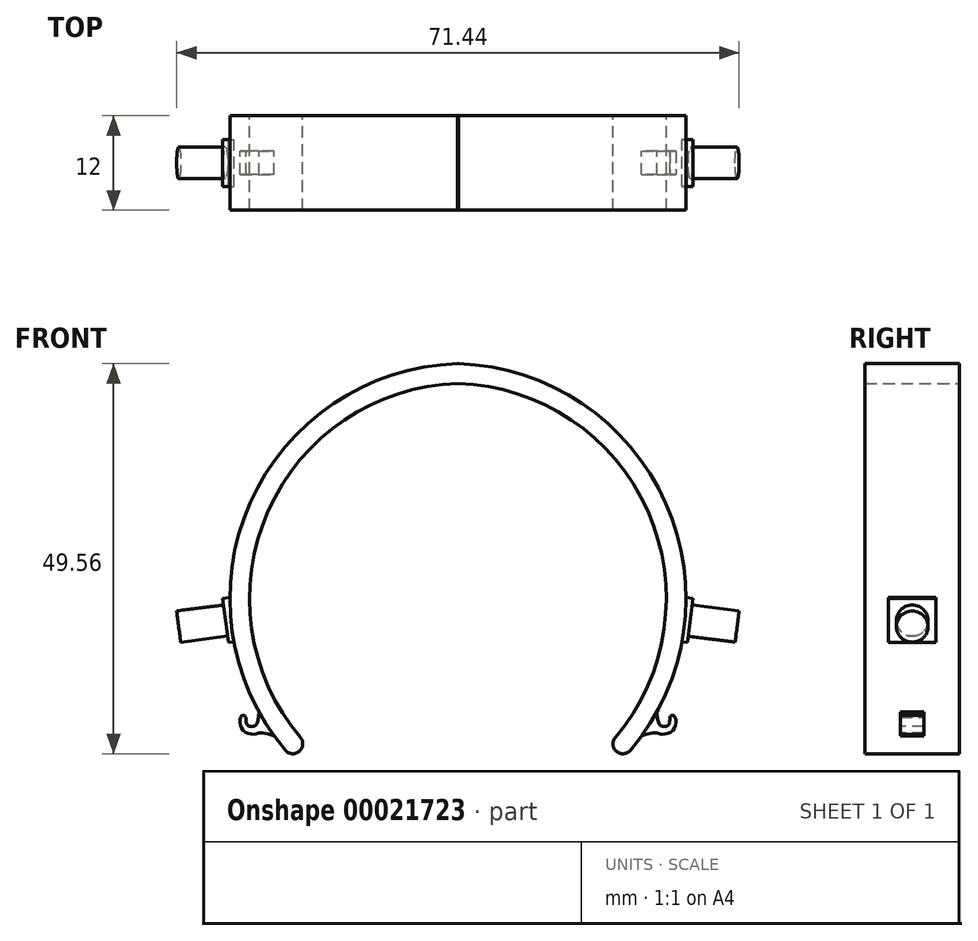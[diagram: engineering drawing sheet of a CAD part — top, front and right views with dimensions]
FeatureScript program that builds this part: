
annotation { "Feature Type Name" : "Feature", "Feature Type Description" : "" }
export const myFeature = defineFeature(function(context is Context, id is Id, definition is map)
    precondition{}
    {
        {
            var Q0;
            Q0=qCreatedBy(makeId("Front.planeOp"),FACE);
            var sketch = newSketch(context, id + "F0", { "sketchPlane" : qUnion([Q0])});
            skCircle(sketch, "E0", {"center": v(0, 0) * mm, "radius": 30 * mm, "construction": true});
            skCircle(sketch, "E1", {"center": v(0, 0) * mm, "radius": 25 * mm, "construction": true});
            skLineSegment(sketch, "E2", {"start": v(-45.65, -15) * mm, "end": v(51.75, -15) * mm, "construction": true});
            skArc(sketch, "E3", {"start": v(20, -15) * mm, "mid": v(24.11, 13.77) * mm, "end": v(0, 30) * mm});
            skArc(sketch, "E4.0", {"start": v(21.9, -16.61) * mm, "mid": v(26.4, 14.79) * mm, "end": v(0.08, 32.5) * mm});
            skLineSegment(sketch, "E5", {"start": v(0.08, 32.5) * mm, "end": v(0, 32.5) * mm});
            skArc(sketch, "E6", {"start": v(20, -15) * mm, "mid": v(20.15, -16.76) * mm, "end": v(21.9, -16.61) * mm});
            skArc(sketch, "E7.MirrorCS", {"start": v(-21.9, -16.61) * mm, "mid": v(-26.4, 14.79) * mm, "end": v(-0.08, 32.5) * mm});
            skLineSegment(sketch, "E8.MirrorCS", {"start": v(-0.08, 32.5) * mm, "end": v(0, 32.5) * mm});
            skArc(sketch, "E9.MirrorCS", {"start": v(-20, -15) * mm, "mid": v(-24.11, 13.77) * mm, "end": v(0, 30) * mm});
            skArc(sketch, "E10.MirrorCS", {"start": v(-20, -15) * mm, "mid": v(-20.15, -16.76) * mm, "end": v(-21.9, -16.61) * mm});
            skSolve(sketch);
        }
        {
            var Q0;
            Q0 = qSketchRegion(id + "F0", true);
            extrude(context, id + "F1", {"entities" : qUnion([Q0]), "depth" : 12 * mm});
        }
        {
            var Q0;
            Q0=makeQuery(id+"F1.opExtrude","CAP_FACE",FACE,{"disambiguationData":[OSD([sQuery(id+"F0.wireOp",EDGE,"E5"),sQuery(id+"F0.wireOp",EDGE,"E6"),sQuery(id+"F0.wireOp",EDGE,"E8.MirrorCS"),sQuery(id+"F0.wireOp",EDGE,"E3"),sQuery(id+"F0.wireOp",EDGE,"E4.0"),sQuery(id+"F0.wireOp",EDGE,"E9.MirrorCS"),sQuery(id+"F0.wireOp",EDGE,"E7.MirrorCS"),sQuery(id+"F0.wireOp",EDGE,"E10.MirrorCS")])],"isStart":false});
            var Q1;
            Q1=makeQuery(id+"F1.opExtrude","CAP_FACE",FACE,{"disambiguationData":[OSD([sQuery(id+"F0.wireOp",EDGE,"E5"),sQuery(id+"F0.wireOp",EDGE,"E6"),sQuery(id+"F0.wireOp",EDGE,"E8.MirrorCS"),sQuery(id+"F0.wireOp",EDGE,"E3"),sQuery(id+"F0.wireOp",EDGE,"E4.0"),sQuery(id+"F0.wireOp",EDGE,"E9.MirrorCS"),sQuery(id+"F0.wireOp",EDGE,"E7.MirrorCS"),sQuery(id+"F0.wireOp",EDGE,"E10.MirrorCS")])],"isStart":true});
            cPlane(context, id + "F2", {"entities" : qUnion([Q0, Q1]), "cplaneType" : CPlaneType.MID_PLANE, "offset" : 6 * mm, "oppositeDirection" : true, "width" : 150 * mm, "height" : 150 * mm});
        }
        {
            var Q0;
            Q0=qCreatedBy(id+"F2.planeOp",FACE);
            var sketch = newSketch(context, id + "F3", { "sketchPlane" : qUnion([Q0])});
            skArc(sketch, "E11.0", {"start": v(21.9, -16.61) * mm, "mid": v(26.4, 14.79) * mm, "end": v(0.08, 32.5) * mm});
            skFitSpline(sketch, "E12", {"points": [v(25.27, -11.73) * mm, v(25.74, -13.46) * mm, v(26.7, -13.43) * mm, v(26.92, -12.45) * mm], "startDerivative": vector(0.39, -5.42) * mm, "endDerivative": vector(-0.06, 3.86) * mm});
            skFitSpline(sketch, "E13", {"points": [v(26.92, -12.45) * mm, v(27.21, -12.16) * mm, v(27.6, -12.45) * mm, v(27.29, -14.1) * mm, v(25.69, -14.57) * mm, v(25.07, -14.4) * mm, v(23.33, -14.8) * mm], "startDerivative": vector(2.47, 3.81) * mm, "endDerivative": vector(-9.3, -2.95) * mm});
            skSolve(sketch);
        }
        {
            var Q0;
            Q0 = qSketchRegion(id + "F3", true);
            extrude(context, id + "F4", {"entities" : qUnion([Q0]), "operationType" : NewBodyOperationType.ADD, "depth" : 3 * mm, "symmetric" : true});
        }
        {
            var Q0;
            Q0=makeQuery(id+"F1.opExtrude","SWEPT_BODY",BODY,{"disambiguationData":[OSD([sQuery(id+"F0.wireOp",EDGE,"E5"),sQuery(id+"F0.wireOp",EDGE,"E6"),sQuery(id+"F0.wireOp",EDGE,"E8.MirrorCS"),sQuery(id+"F0.wireOp",EDGE,"E3"),sQuery(id+"F0.wireOp",EDGE,"E4.0"),sQuery(id+"F0.wireOp",EDGE,"E9.MirrorCS"),sQuery(id+"F0.wireOp",EDGE,"E7.MirrorCS"),sQuery(id+"F0.wireOp",EDGE,"E10.MirrorCS")])]});
            var Q1;
            Q1=qCreatedBy(makeId("Right.planeOp"),FACE);
            mirror(context, id + "F5", {"operationType" : NewBodyOperationType.ADD, "entities" : qUnion([Q0]), "mirrorPlane" : qUnion([Q1])});
        }
        {
            var Q0;
            Q0=qCreatedBy(id+"F2.planeOp",FACE);
            var sketch = newSketch(context, id + "F6", { "sketchPlane" : qUnion([Q0])});
            skCircle(sketch, "E14", {"center": v(0, 0) * mm, "radius": 30 * mm, "construction": true});
            skLineSegment(sketch, "E15", {"start": v(27.62, -2.74) * mm, "end": v(28.34, 2.87) * mm});
            skLineSegment(sketch, "E16", {"start": v(28.34, 2.87) * mm, "end": v(29.88, 2.68) * mm});
            skLineSegment(sketch, "E17", {"start": v(29.88, 2.68) * mm, "end": v(29.16, -2.94) * mm});
            skLineSegment(sketch, "E18", {"start": v(29.16, -2.94) * mm, "end": v(27.62, -2.74) * mm});
            skLineSegment(sketch, "E19", {"start": v(29.52, -0.13) * mm, "end": v(33.04, -0.59) * mm, "construction": true});
            skLineSegment(sketch, "E20", {"start": v(29.77, 1.85) * mm, "end": v(35.72, 1.08) * mm});
            skLineSegment(sketch, "E21.MirrorCS", {"start": v(29.26, -2.12) * mm, "end": v(35.21, -2.88) * mm});
            skLineSegment(sketch, "E22", {"start": v(35.72, 1.08) * mm, "end": v(35.21, -2.88) * mm});
            skLineSegment(sketch, "E23.MirrorCS", {"start": v(-28.34, 2.87) * mm, "end": v(-29.88, 2.68) * mm});
            skLineSegment(sketch, "E24.MirrorCS", {"start": v(-27.62, -2.74) * mm, "end": v(-28.34, 2.87) * mm});
            skLineSegment(sketch, "E25.MirrorCS", {"start": v(-29.16, -2.94) * mm, "end": v(-27.62, -2.74) * mm});
            skLineSegment(sketch, "E26.MirrorCS", {"start": v(-29.88, 2.68) * mm, "end": v(-29.16, -2.94) * mm});
            skLineSegment(sketch, "E27.MirrorCS", {"start": v(-29.26, -2.12) * mm, "end": v(-35.21, -2.88) * mm});
            skLineSegment(sketch, "E28.MirrorCS", {"start": v(-29.77, 1.85) * mm, "end": v(-35.72, 1.08) * mm});
            skLineSegment(sketch, "E29.MirrorCS", {"start": v(-35.72, 1.08) * mm, "end": v(-35.21, -2.88) * mm});
            skSolve(sketch);
        }
        {
            var Q0;
            Q0 = qSketchRegion(id + "F6", true);
            extrude(context, id + "F7", {"entities" : qUnion([Q0]), "operationType" : NewBodyOperationType.ADD, "depth" : 6 * mm, "symmetric" : true});
        }
        {
            var Q0;
            Q0=makeQuery(id+"F7.opExtrude","SWEPT_FACE",FACE,{"disambiguationData":[OSD([sQuery(id+"F6.wireOp",EDGE,"E22")])]});
            var sketch = newSketch(context, id + "F8", { "sketchPlane" : qUnion([Q0])});
            skLineSegment(sketch, "E30", {"start": v(-9, 3.65) * mm, "end": v(-3, 3.65) * mm, "construction": true});
            skLineSegment(sketch, "E31", {"start": v(-6, 5.65) * mm, "end": v(-6, 1.65) * mm, "construction": true});
            skCircle(sketch, "E32", {"center": v(-6, 3.65) * mm, "radius": 2 * mm});
            skLineSegment(sketch, "E33.rect.bottom", {"start": v(-3, 1.65) * mm, "end": v(-9, 1.65) * mm});
            skLineSegment(sketch, "E33.rect.top", {"start": v(-3, 5.65) * mm, "end": v(-9, 5.65) * mm});
            skLineSegment(sketch, "E33.rect.left", {"start": v(-3, 1.65) * mm, "end": v(-3, 5.65) * mm});
            skLineSegment(sketch, "E33.rect.right", {"start": v(-9, 1.65) * mm, "end": v(-9, 5.65) * mm});
            skSolve(sketch);
        }
        {
            var Q0;
            {var subQ0=sQuery(id+"F8.wireOp",EDGE,"E33.rect.right");Q0=makeQuery(id+"F8.imprint","IMPRINT",FACE,{"disambiguationData":[TD([[makeQuery(id+"F8.imprint","IMPRINT",EDGE,{"derivedFrom":subQ0}),1.0]])]});}
            var Q1;
            {var subQ0=sQuery(id+"F8.wireOp",EDGE,"E33.rect.left");Q1=makeQuery(id+"F8.imprint","IMPRINT",FACE,{"disambiguationData":[TD([[makeQuery(id+"F8.imprint","IMPRINT",EDGE,{"derivedFrom":subQ0}),-1.0]])]});}
            extrude(context, id + "F9", {"entities" : qUnion([Q0, Q1]), "operationType" : NewBodyOperationType.REMOVE, "oppositeDirection" : true, "depth" : 6 * mm});
        }
        {
            var Q0;
            Q0=makeQuery(id+"F7.opExtrude","SWEPT_FACE",FACE,{"disambiguationData":[OSD([sQuery(id+"F6.wireOp",EDGE,"E29.MirrorCS")])]});
            var sketch = newSketch(context, id + "F10", { "sketchPlane" : qUnion([Q0])});
            skLineSegment(sketch, "E34", {"start": v(3, 3.65) * mm, "end": v(9, 3.65) * mm, "construction": true});
            skLineSegment(sketch, "E35", {"start": v(6, 5.65) * mm, "end": v(6, 1.65) * mm, "construction": true});
            skCircle(sketch, "E36", {"center": v(6, 3.65) * mm, "radius": 2 * mm});
            skLineSegment(sketch, "E37.rect.bottom", {"start": v(9, 1.65) * mm, "end": v(3, 1.65) * mm});
            skLineSegment(sketch, "E37.rect.top", {"start": v(9, 5.65) * mm, "end": v(3, 5.65) * mm});
            skLineSegment(sketch, "E37.rect.left", {"start": v(9, 1.65) * mm, "end": v(9, 5.65) * mm});
            skLineSegment(sketch, "E37.rect.right", {"start": v(3, 1.65) * mm, "end": v(3, 5.65) * mm});
            skSolve(sketch);
        }
        {
            var Q0;
            {var subQ0=sQuery(id+"F10.wireOp",EDGE,"E37.rect.right");Q0=makeQuery(id+"F10.imprint","IMPRINT",FACE,{"disambiguationData":[TD([[makeQuery(id+"F10.imprint","IMPRINT",EDGE,{"derivedFrom":subQ0}),1.0]])]});}
            var Q1;
            {var subQ0=sQuery(id+"F10.wireOp",EDGE,"E37.rect.left");Q1=makeQuery(id+"F10.imprint","IMPRINT",FACE,{"disambiguationData":[TD([[makeQuery(id+"F10.imprint","IMPRINT",EDGE,{"derivedFrom":subQ0}),-1.0]])]});}
            extrude(context, id + "F11", {"entities" : qUnion([Q0, Q1]), "operationType" : NewBodyOperationType.REMOVE, "oppositeDirection" : true, "depth" : 6 * mm});
        }
    });
